# Revit family: TOR1_63_UN_Surface-mounted_ETK
name_source: partatom
category: Lighting Fixtures
revit_build: Autodesk Revit 2017 (Build: 20190508_0315(x64)
units: mm (PartAtom-declared; Revit-internal decimal feet)

## family parameters
Always vertical = No
Cut with Voids When Loaded = No
Light Source = No
OmniClass Number = 23.80.70.00
OmniClass Title = Lighting
Part Type = Normal
Room Calculation Point = Yes
Round Connector Dimension = Use Diameter
Shared = No
Work Plane-Based = No

## types (24) — shared parameters
Assembly Code = 63.0
Description = Surface-mounted luminaire
IfcExportAs = IfcLightFixtureType
IfcExportType = USERDEFINED
Lamp = LED
Luminaire_Body_Material = PPS Plastic
Luminaire_Cap_Material = PPS Plastic
Manufacturer = ETK licht B.V.
Model = TOR.1
URL = https://www.etk.nl
Voltage = 230 V

## per-type parameters (varying)
| type | Apparent Load | Geometry | Lightsource | Wattage Comments |
| TOR.1600.20 - 16W / 2250lm / 3000K | 16 VA | TOR1 - Geometry : TOR.1 - Length 1277mm | TOR.1 - Lightsource : TOR.1600.20 - 16W / 2250lm / 3000K | 16W |
| TOR.1603.20 - 16W / 2250lm / 3000K | 16 VA | TOR1 - Geometry : TOR.1 - Length 1277mm | TOR.1 - Lightsource : TOR.1603.20 - 16W / 2250lm / 3000K | 16W |
| TOR.1610.20 - 16W / 2350lm / 4000K | 16 VA | TOR1 - Geometry : TOR.1 - Length 1277mm | TOR.1 - Lightsource : TOR.1610.20 - 16W / 2350lm / 4000K | 16W |
| TOR.1613.20 - 16W / 2350lm / 4000K | 16 VA | TOR1 - Geometry : TOR.1 - Length 1277mm | TOR.1 - Lightsource : TOR.1613.20 - 16W / 2350lm / 4000K | 16W |
| TOR.1620.20 - 33W / 4400lm / 3000K | 33 VA | TOR1 - Geometry : TOR.1 - Length 1277mm | TOR.1 - Lightsource : TOR.1620.20 - 33W / 4400lm / 3000K | 33W |
| TOR.1623.20 - 33W / 4400lm / 3000K | 33 VA | TOR1 - Geometry : TOR.1 - Length 1277mm | TOR.1 - Lightsource : TOR.1623.20 - 33W / 4400lm / 3000K | 33W |
| TOR.1630.20 - 33W / 4600lm / 4000K | 33 VA | TOR1 - Geometry : TOR.1 - Length 1277mm | TOR.1 - Lightsource : TOR.1630.20 - 33W / 4600lm / 4000K | 33W |
| TOR.1633.20 - 33W / 4400lm / 4000K | 33 VA | TOR1 - Geometry : TOR.1 - Length 1277mm | TOR.1 - Lightsource : TOR.1633.20 - 33W / 4400lm / 4000K | 33W |
| TOR.1640.20 - 43W / 5950lm / 3000K | 43 VA | TOR1 - Geometry : TOR.1 - Length 1277mm | TOR.1 - Lightsource : TOR.1640.20 - 43W / 5950lm / 3000K | 43W |
| TOR.1643.20 - 43W / 5950lm / 3000K | 43 VA | TOR1 - Geometry : TOR.1 - Length 1277mm | TOR.1 - Lightsource : TOR.1643.20 - 43W / 5950lm / 3000K | 43W |
| TOR.1650.20 - 43W / 6250lm / 4000K | 43 VA | TOR1 - Geometry : TOR.1 - Length 1277mm | TOR.1 - Lightsource : TOR.1650.20 - 43W / 6250lm / 4000K | 43W |
| TOR.1653.20 - 43W / 6250lm / 4000K | 43 VA | TOR1 - Geometry : TOR.1 - Length 1277mm | TOR.1 - Lightsource : TOR.1653.20 - 43W / 6250lm / 4000K | 43W |
| TOR.1700.20 - 26W / 3550lm / 3000K | 26 VA | TOR1 - Geometry : TOR.1 - Length 1577mm | TOR.1 - Lightsource : TOR.1700.20 - 26W / 3550lm / 3000K | 26W |
| TOR.1703.20 - 26W / 3550lm / 3000K | 26 VA | TOR1 - Geometry : TOR.1 - Length 1577mm | TOR.1 - Lightsource : TOR.1703.20 - 26W / 3550lm / 3000K | 26W |
| TOR.1710.20 - 26W / 3700lm / 4000K | 26 VA | TOR1 - Geometry : TOR.1 - Length 1577mm | TOR.1 - Lightsource : TOR.1710.20 - 26W / 3700lm / 4000K | 26W |
| TOR.1713.20 - 26W / 3700lm / 4000K | 26 VA | TOR1 - Geometry : TOR.1 - Length 1577mm | TOR.1 - Lightsource : TOR.1713.20 - 26W / 3700lm / 4000K | 26W |
| TOR.1720.20 - 50W / 6450lm / 3000K | 50 VA | TOR1 - Geometry : TOR.1 - Length 1577mm | TOR.1 - Lightsource : TOR.1720.20 - 50W / 6450lm / 3000K | 50W |
| TOR.1723.20 - 50W / 6450lm / 3000K | 50 VA | TOR1 - Geometry : TOR.1 - Length 1577mm | TOR.1 - Lightsource : TOR.1723.20 - 50W / 6450lm / 3000K | 50W |
| TOR.1730.20 - 50W / 6750lm / 4000K | 50 VA | TOR1 - Geometry : TOR.1 - Length 1577mm | TOR.1 - Lightsource : TOR.1730.20 - 50W / 6750lm / 4000K | 50W |
| TOR.1733.20 - 50W / 6750lm / 4000K | 50 VA | TOR1 - Geometry : TOR.1 - Length 1577mm | TOR.1 - Lightsource : TOR.1733.20 - 50W / 6750lm / 4000K | 50W |
| TOR.1740.20 - 61W / 8500lm / 3000K | 61 VA | TOR1 - Geometry : TOR.1 - Length 1577mm | TOR.1 - Lightsource : TOR.1740.20 - 61W / 8500lm / 3000K | 61W |
| TOR.1743.20 - 61W / 8500lm / 3000K | 61 VA | TOR1 - Geometry : TOR.1 - Length 1577mm | TOR.1 - Lightsource : TOR.1743.20 - 61W / 8500lm / 3000K | 61W |
| TOR.1750.20 - 61W / 9000lm / 4000K | 61 VA | TOR1 - Geometry : TOR.1 - Length 1577mm | TOR.1 - Lightsource : TOR.1750.20 - 61W / 9000lm / 4000K | 61W |
| TOR.1753.20 - 61W / 9000lm / 4000K | 61 VA | TOR1 - Geometry : TOR.1 - Length 1577mm | TOR.1 - Lightsource : TOR.1753.20 - 61W / 9000lm / 4000K | 61W |

## geometry (parser evidence)
native form markers: Sweep x16
no freeform markers — native parametric forms only
